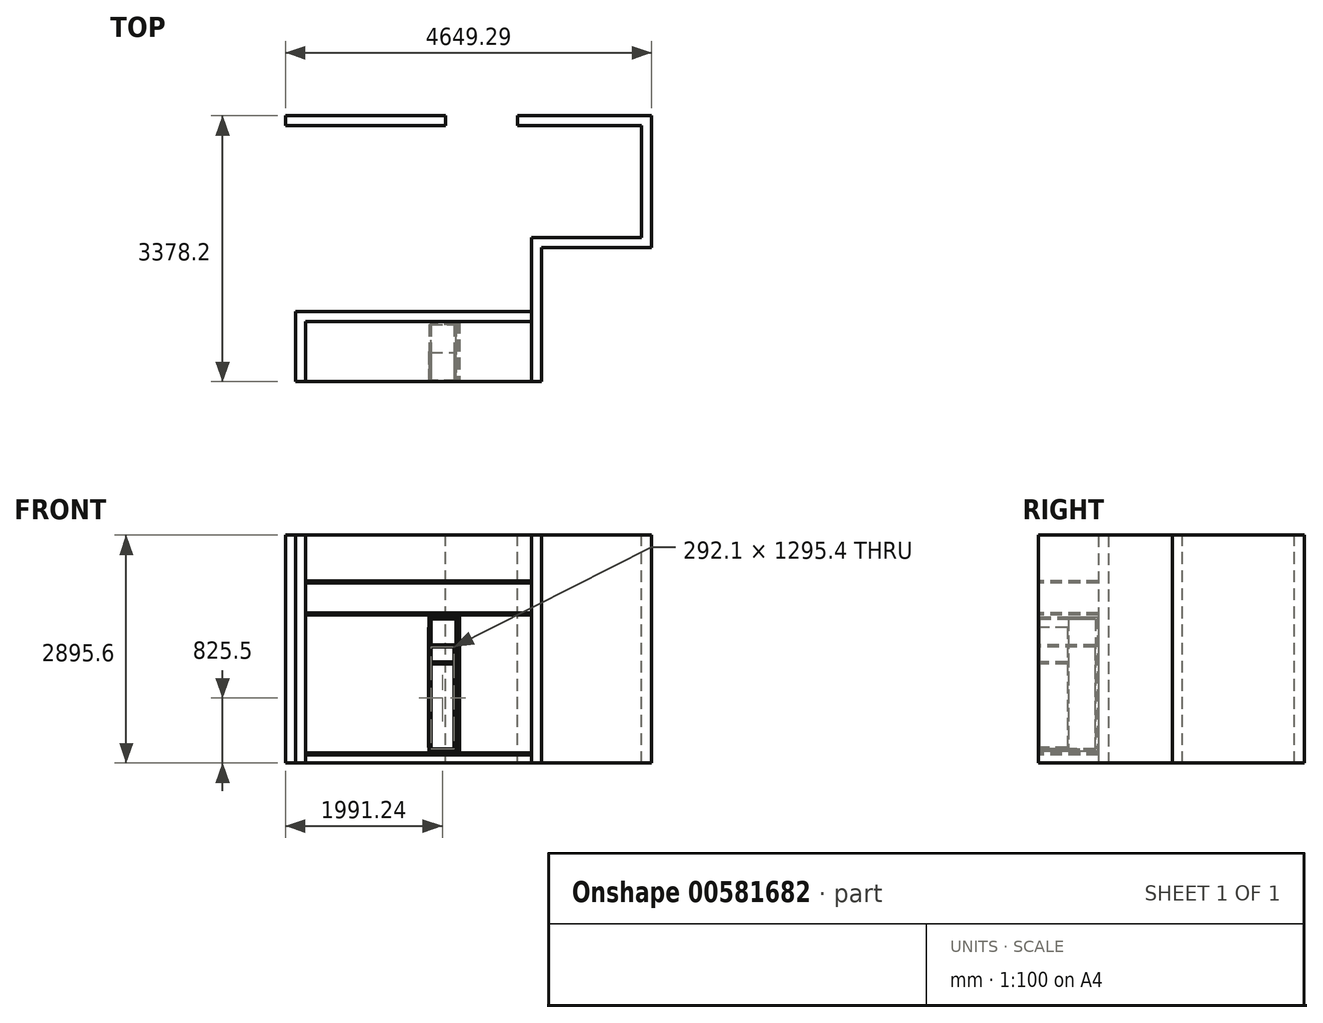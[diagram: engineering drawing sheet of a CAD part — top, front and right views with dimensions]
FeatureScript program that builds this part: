
annotation { "Feature Type Name" : "Feature", "Feature Type Description" : "" }
export const myFeature = defineFeature(function(context is Context, id is Id, definition is map)
    precondition{}
    {
        {
            var Q0;
            Q0=qCreatedBy(makeId("Top.planeOp"),FACE);
            var sketch = newSketch(context, id + "F0", { "sketchPlane" : qUnion([Q0])});
            skLineSegment(sketch, "E0.bottom", {"start": v(-1072.65, 1.26) * mm, "end": v(1797.55, 1.26) * mm});
            skLineSegment(sketch, "E0.top", {"start": v(-1072.65, -125.74) * mm, "end": v(1797.55, -125.74) * mm});
            skLineSegment(sketch, "E0.left", {"start": v(-1072.65, 1.26) * mm, "end": v(-1072.65, -125.74) * mm});
            skLineSegment(sketch, "E0.right", {"start": v(1797.55, 1.26) * mm, "end": v(1797.55, -125.74) * mm});
            skLineSegment(sketch, "E1.bottom", {"start": v(-1072.65, 1.26) * mm, "end": v(-1199.65, 1.26) * mm});
            skLineSegment(sketch, "E1.top", {"start": v(-1072.65, -887.74) * mm, "end": v(-1199.65, -887.74) * mm});
            skLineSegment(sketch, "E1.left", {"start": v(-1072.65, 1.26) * mm, "end": v(-1072.65, -887.74) * mm});
            skLineSegment(sketch, "E1.right", {"start": v(-1199.65, 1.26) * mm, "end": v(-1199.65, -887.74) * mm});
            skSolve(sketch);
        }
        {
            var Q0;
            {var subQ3=sQuery(id+"F0.wireOp",EDGE,"E1.bottom");Q0=makeQuery(id+"F0.imprint","IMPRINT",FACE,{"disambiguationData":[TD([[makeQuery(id+"F0.imprint","IMPRINT",EDGE,{"derivedFrom":subQ3}),1.0]])]});}
            var Q1;
            {var subQ0=sQuery(id+"F0.wireOp",EDGE,"E0.bottom");Q1=makeQuery(id+"F0.imprint","IMPRINT",FACE,{"disambiguationData":[TD([[makeQuery(id+"F0.imprint","IMPRINT",EDGE,{"derivedFrom":subQ0}),-1.0]])]});}
            extrude(context, id + "F1", {"entities" : qUnion([Q0, Q1]), "depth" : 2895.6 * mm, "offsetDistance" : 25.4 * mm});
        }
        {
            var Q0;
            Q0=makeQuery(id+"F1.opExtrude","CAP_FACE",FACE,{"disambiguationData":[OSD([sQuery(id+"F0.wireOp",EDGE,"E0.bottom"),sQuery(id+"F0.wireOp",EDGE,"E0.top"),sQuery(id+"F0.wireOp",EDGE,"E0.right"),sQuery(id+"F0.wireOp",EDGE,"E1.bottom"),sQuery(id+"F0.wireOp",EDGE,"E1.top"),sQuery(id+"F0.wireOp",EDGE,"E1.left"),sQuery(id+"F0.wireOp",EDGE,"E1.right")])],"isStart":false});
            var sketch = newSketch(context, id + "F2", { "sketchPlane" : qUnion([Q0])});
            skLineSegment(sketch, "E2.bottom", {"start": v(-1072.65, -125.74) * mm, "end": v(1797.55, -125.74) * mm});
            skLineSegment(sketch, "E2.top", {"start": v(-1072.65, -887.74) * mm, "end": v(1797.55, -887.74) * mm});
            skLineSegment(sketch, "E2.left", {"start": v(-1072.65, -125.74) * mm, "end": v(-1072.65, -887.74) * mm});
            skLineSegment(sketch, "E2.right", {"start": v(1797.55, -125.74) * mm, "end": v(1797.55, -887.74) * mm});
            skSolve(sketch);
        }
        {
            var Q0;
            Q0=makeQuery(id+"F2.imprint","IMPRINT",FACE,{"disambiguationData":[TD([[makeQuery(id+"F2.imprint","IMPRINT",EDGE,{"derivedFrom":sQuery(id+"F2.wireOp",EDGE,"E2.bottom")}),-1.0]])]});
            extrude(context, id + "F3", {"entities" : qUnion([Q0]), "operationType" : NewBodyOperationType.ADD, "depth" : 25.4 * mm, "offsetDistance" : 25.4 * mm});
        }
        {
            var Q0;
            Q0=makeQuery(id+"F3.opExtrude","SWEPT_BODY",BODY,{"disambiguationData":[OSD([sQuery(id+"F2.wireOp",EDGE,"E2.bottom"),sQuery(id+"F2.wireOp",EDGE,"E2.top"),sQuery(id+"F2.wireOp",EDGE,"E2.left"),sQuery(id+"F2.wireOp",EDGE,"E2.right")])]});
            transform(context, id + "F4", {"entities" : qUnion([Q0]), "transformType" : TransformType.TRANSLATION_3D, "dx" : 0 * mm, "dy" : 0 * mm, "dz" : -609.6 * mm, "makeCopy" : false});
        }
        {
            var Q0;
            Q0=makeQuery(id+"F3.opExtrude","SWEPT_BODY",BODY,{"disambiguationData":[OSD([sQuery(id+"F2.wireOp",EDGE,"E2.bottom"),sQuery(id+"F2.wireOp",EDGE,"E2.top"),sQuery(id+"F2.wireOp",EDGE,"E2.left"),sQuery(id+"F2.wireOp",EDGE,"E2.right")])]});
            transform(context, id + "F5", {"entities" : qUnion([Q0]), "transformType" : TransformType.TRANSLATION_3D, "dx" : 0 * mm, "dy" : 0 * mm, "dz" : -406.4 * mm, "makeCopy" : true});
        }
        {
            var Q0;
            Q0=makeQuery(id+"F5.opPattern","COPY",FACE,{"derivedFrom":makeQuery(id+"F3.opExtrude","SWEPT_FACE",FACE,{"disambiguationData":[OSD([sQuery(id+"F2.wireOp",EDGE,"E2.top")])]}),"instanceName":"1"});
            var sketch = newSketch(context, id + "F6", { "sketchPlane" : qUnion([Q0])});
            skLineSegment(sketch, "E3.bottom", {"start": v(793.61, 1879.6) * mm, "end": v(819.01, 1879.6) * mm});
            skLineSegment(sketch, "E3.top", {"start": v(793.61, 127) * mm, "end": v(819.01, 127) * mm});
            skLineSegment(sketch, "E3.left", {"start": v(793.61, 1879.6) * mm, "end": v(793.61, 127) * mm});
            skLineSegment(sketch, "E3.right", {"start": v(819.01, 1879.6) * mm, "end": v(819.01, 127) * mm});
            skSolve(sketch);
        }
        {
            var Q0;
            Q0=makeQuery(id+"F6.imprint","IMPRINT",FACE,{"disambiguationData":[TD([[makeQuery(id+"F6.imprint","IMPRINT",EDGE,{"derivedFrom":sQuery(id+"F6.wireOp",EDGE,"E3.bottom")}),-1.0]])]});
            extrude(context, id + "F7", {"entities" : qUnion([Q0]), "depth" : -762 * mm, "offsetDistance" : 25.4 * mm});
        }
        {
            var Q0;
            Q0=makeQuery(id+"F5.opPattern","COPY",BODY,{"derivedFrom":makeQuery(id+"F3.opExtrude","SWEPT_BODY",BODY,{"disambiguationData":[OSD([sQuery(id+"F2.wireOp",EDGE,"E2.bottom"),sQuery(id+"F2.wireOp",EDGE,"E2.top"),sQuery(id+"F2.wireOp",EDGE,"E2.left"),sQuery(id+"F2.wireOp",EDGE,"E2.right")])]}),"instanceName":"1"});
            transform(context, id + "F8", {"entities" : qUnion([Q0]), "transformType" : TransformType.TRANSLATION_3D, "dx" : 0 * mm, "dy" : 0 * mm, "dz" : -1778 * mm, "makeCopy" : true});
        }
        {
            var Q0;
            Q0=makeQuery(id+"F7.opExtrude","SWEPT_BODY",BODY,{"disambiguationData":[OSD([sQuery(id+"F6.wireOp",EDGE,"E3.bottom"),sQuery(id+"F6.wireOp",EDGE,"E3.top"),sQuery(id+"F6.wireOp",EDGE,"E3.left"),sQuery(id+"F6.wireOp",EDGE,"E3.right")])]});
            transform(context, id + "F9", {"entities" : qUnion([Q0]), "transformType" : TransformType.TRANSLATION_3D, "dx" : 64.13 * mm, "dy" : 0 * mm, "dz" : 0 * mm, "makeCopy" : false});
        }
        {
            var Q0;
            Q0=makeQuery(id+"F8.opPattern","COPY",FACE,{"derivedFrom":makeQuery(id+"F5.opPattern","COPY",FACE,{"derivedFrom":makeQuery(id+"F3.opExtrude","CAP_FACE",FACE,{"disambiguationData":[OSD([sQuery(id+"F2.wireOp",EDGE,"E2.bottom"),sQuery(id+"F2.wireOp",EDGE,"E2.top"),sQuery(id+"F2.wireOp",EDGE,"E2.left"),sQuery(id+"F2.wireOp",EDGE,"E2.right")])],"isStart":false}),"instanceName":"1"}),"instanceName":"1"});
            var sketch = newSketch(context, id + "F10", { "sketchPlane" : qUnion([Q0])});
            skLineSegment(sketch, "E4.bottom", {"start": v(831.7, -876.48) * mm, "end": v(488.8, -876.48) * mm});
            skLineSegment(sketch, "E4.top", {"start": v(831.7, -139.88) * mm, "end": v(488.8, -139.88) * mm});
            skLineSegment(sketch, "E4.left", {"start": v(831.7, -876.48) * mm, "end": v(831.7, -139.88) * mm});
            skLineSegment(sketch, "E4.right", {"start": v(488.8, -876.48) * mm, "end": v(488.8, -139.88) * mm});
            skSolve(sketch);
        }
        {
            var Q0;
            Q0=makeQuery(id+"F10.imprint","IMPRINT",FACE,{"disambiguationData":[TD([[makeQuery(id+"F10.imprint","IMPRINT",EDGE,{"derivedFrom":sQuery(id+"F10.wireOp",EDGE,"E4.bottom")}),-1.0]])]});
            extrude(context, id + "F11", {"entities" : qUnion([Q0]), "depth" : 1701.8 * mm, "offsetDistance" : 25.4 * mm});
        }
        {
            var Q0;
            Q0=makeQuery(id+"F11.opExtrude","SWEPT_BODY",BODY,{"disambiguationData":[OSD([sQuery(id+"F10.wireOp",EDGE,"E4.bottom"),sQuery(id+"F10.wireOp",EDGE,"E4.top"),sQuery(id+"F10.wireOp",EDGE,"E4.left"),sQuery(id+"F10.wireOp",EDGE,"E4.right")])]});
            transform(context, id + "F12", {"entities" : qUnion([Q0]), "transformType" : TransformType.TRANSLATION_3D, "dx" : 3.25 * mm, "dy" : 0 * mm, "dz" : 25.4 * mm, "makeCopy" : false});
        }
        {
            var Q0;
            Q0=makeQuery(id+"F11.opExtrude","SWEPT_FACE",FACE,{"disambiguationData":[OSD([sQuery(id+"F10.wireOp",EDGE,"E4.bottom")])]});
            shell(context, id + "F13", {"entities" : qUnion([Q0]), "thickness" : 25.4 * mm});
        }
        {
            var Q0;
            Q0=makeQuery(id+"F11.opExtrude","SWEPT_FACE",FACE,{"disambiguationData":[OSD([sQuery(id+"F10.wireOp",EDGE,"E4.right")])]});
            var sketch = newSketch(context, id + "F14", { "sketchPlane" : qUnion([Q0])});
            skLineSegment(sketch, "E5.bottom", {"start": v(139.88, 1854.2) * mm, "end": v(508.18, 1854.2) * mm});
            skLineSegment(sketch, "E5.top", {"start": v(139.88, 152.4) * mm, "end": v(508.18, 152.4) * mm});
            skLineSegment(sketch, "E5.left", {"start": v(139.88, 1854.2) * mm, "end": v(139.88, 152.4) * mm});
            skLineSegment(sketch, "E5.right", {"start": v(508.18, 1854.2) * mm, "end": v(508.18, 152.4) * mm});
            skSolve(sketch);
        }
        {
            var Q0;
            Q0=makeQuery(id+"F14.imprint","IMPRINT",FACE,{"disambiguationData":[TD([[makeQuery(id+"F14.imprint","IMPRINT",EDGE,{"derivedFrom":sQuery(id+"F14.wireOp",EDGE,"E5.bottom")}),1.0]])]});
            extrude(context, id + "F15", {"entities" : qUnion([Q0]), "operationType" : NewBodyOperationType.REMOVE, "oppositeDirection" : true, "depth" : 25.4 * mm, "offsetDistance" : 25.4 * mm});
        }
        {
            var Q0;
            Q0=makeQuery(id+"F13.opShell","OFFSET_FACE",FACE,{"disambiguationData":[OSD([sQuery(id+"F10.wireOp",EDGE,"E4.left")])]});
            extrude(context, id + "F16", {"entities" : qUnion([Q0]), "operationType" : NewBodyOperationType.REMOVE, "oppositeDirection" : true, "depth" : 25.4 * mm, "offsetDistance" : 25.4 * mm});
        }
        {
            var Q0;
            Q0=makeQuery(id+"F11.opExtrude","SWEPT_FACE",FACE,{"disambiguationData":[OSD([sQuery(id+"F10.wireOp",EDGE,"E4.right")])]});
            var sketch = newSketch(context, id + "F17", { "sketchPlane" : qUnion([Q0])});
            skLineSegment(sketch, "E6.bottom", {"start": v(1637.69, 1724.74) * mm, "end": v(1993.29, 1724.74) * mm});
            skLineSegment(sketch, "E6.top", {"start": v(1637.69, 200.74) * mm, "end": v(1993.29, 200.74) * mm});
            skLineSegment(sketch, "E6.left", {"start": v(1637.69, 1724.74) * mm, "end": v(1637.69, 200.74) * mm});
            skLineSegment(sketch, "E6.right", {"start": v(1993.29, 1724.74) * mm, "end": v(1993.29, 200.74) * mm});
            skSolve(sketch);
        }
        {
            var Q0;
            Q0=makeQuery(id+"F17.imprint","IMPRINT",FACE,{"disambiguationData":[TD([[makeQuery(id+"F17.imprint","IMPRINT",EDGE,{"derivedFrom":sQuery(id+"F17.wireOp",EDGE,"E6.bottom")}),-1.0]])]});
            extrude(context, id + "F18", {"entities" : qUnion([Q0]), "depth" : 6.35 * mm, "offsetDistance" : 25.4 * mm});
        }
        {
            var Q0;
            Q0=makeQuery(id+"F18.opExtrude","SWEPT_BODY",BODY,{"disambiguationData":[OSD([sQuery(id+"F17.wireOp",EDGE,"E6.bottom"),sQuery(id+"F17.wireOp",EDGE,"E6.top"),sQuery(id+"F17.wireOp",EDGE,"E6.left"),sQuery(id+"F17.wireOp",EDGE,"E6.right")])]});
            transform(context, id + "F19", {"entities" : qUnion([Q0]), "transformType" : TransformType.TRANSLATION_3D, "dx" : 0 * mm, "dy" : 1117.6 * mm, "dz" : 0 * mm, "makeCopy" : false});
        }
        {
            var Q0;
            Q0=makeQuery(id+"F11.opExtrude","SWEPT_FACE",FACE,{"disambiguationData":[OSD([sQuery(id+"F10.wireOp",EDGE,"E4.bottom")])]});
            var sketch = newSketch(context, id + "F20", { "sketchPlane" : qUnion([Q0])});
            skLineSegment(sketch, "E7.bottom", {"start": v(1040.15, 152.4) * mm, "end": v(1383.05, 152.4) * mm});
            skLineSegment(sketch, "E7.top", {"start": v(1040.15, 1498.6) * mm, "end": v(1383.05, 1498.6) * mm});
            skLineSegment(sketch, "E7.left", {"start": v(1040.15, 152.4) * mm, "end": v(1040.15, 1498.6) * mm});
            skLineSegment(sketch, "E7.right", {"start": v(1383.05, 152.4) * mm, "end": v(1383.05, 1498.6) * mm});
            skSolve(sketch);
        }
        {
            var Q0;
            Q0 = qSketchRegion(id + "F20", true);
            extrude(context, id + "F21", {"entities" : qUnion([Q0]), "operationType" : NewBodyOperationType.ADD, "depth" : -711.2 * mm, "offsetDistance" : 25.4 * mm});
        }
        {
            var Q0;
            Q0=makeQuery(id+"F21.opExtrude","CAP_FACE",FACE,{"disambiguationData":[OSD([sQuery(id+"F20.wireOp",EDGE,"E7.bottom"),sQuery(id+"F20.wireOp",EDGE,"E7.top"),sQuery(id+"F20.wireOp",EDGE,"E7.left"),sQuery(id+"F20.wireOp",EDGE,"E7.right")])],"isStart":true});
            shell(context, id + "F22", {"entities" : qUnion([Q0]), "thickness" : 25.4 * mm});
        }
        {
            var Q0;
            Q0=makeQuery(id+"F22.opShell","OFFSET_FACE",FACE,{"disambiguationData":[OSD([sQuery(id+"F20.wireOp",EDGE,"E7.bottom"),sQuery(id+"F20.wireOp",EDGE,"E7.top"),sQuery(id+"F20.wireOp",EDGE,"E7.left"),sQuery(id+"F20.wireOp",EDGE,"E7.right")])]});
            extrude(context, id + "F23", {"entities" : qUnion([Q0]), "operationType" : NewBodyOperationType.REMOVE, "oppositeDirection" : true, "depth" : 25.4 * mm, "offsetDistance" : 25.4 * mm});
        }
        {
            var Q0;
            Q0=makeQuery(id+"F21.opExtrude","SWEPT_BODY",BODY,{"disambiguationData":[OSD([sQuery(id+"F20.wireOp",EDGE,"E7.bottom"),sQuery(id+"F20.wireOp",EDGE,"E7.top"),sQuery(id+"F20.wireOp",EDGE,"E7.left"),sQuery(id+"F20.wireOp",EDGE,"E7.right")])]});
            transform(context, id + "F24", {"entities" : qUnion([Q0]), "transformType" : TransformType.TRANSLATION_3D, "dx" : -548.1 * mm, "dy" : 0 * mm, "dz" : 0 * mm, "makeCopy" : false});
        }
        {
            var Q0;
            Q0=makeQuery(id+"F11.opExtrude","SWEPT_FACE",FACE,{"disambiguationData":[OSD([sQuery(id+"F10.wireOp",EDGE,"E4.bottom")])]});
            var sketch = newSketch(context, id + "F25", { "sketchPlane" : qUnion([Q0])});
            skLineSegment(sketch, "E8.bottom", {"start": v(517.46, 1284.7) * mm, "end": v(809.56, 1284.7) * mm});
            skLineSegment(sketch, "E8.top", {"start": v(517.46, 1259.3) * mm, "end": v(809.56, 1259.3) * mm});
            skLineSegment(sketch, "E8.left", {"start": v(517.46, 1284.7) * mm, "end": v(517.46, 1259.3) * mm});
            skLineSegment(sketch, "E8.right", {"start": v(809.56, 1284.7) * mm, "end": v(809.56, 1259.3) * mm});
            skSolve(sketch);
        }
        {
            var Q0;
            Q0 = qSketchRegion(id + "F25", true);
            extrude(context, id + "F26", {"entities" : qUnion([Q0]), "depth" : -355.6 * mm, "offsetDistance" : 25.4 * mm});
        }
        {
            var Q0;
            Q0=makeQuery(id+"F1.opExtrude","CAP_FACE",FACE,{"disambiguationData":[OSD([sQuery(id+"F0.wireOp",EDGE,"E0.bottom"),sQuery(id+"F0.wireOp",EDGE,"E0.top"),sQuery(id+"F0.wireOp",EDGE,"E0.right"),sQuery(id+"F0.wireOp",EDGE,"E1.bottom"),sQuery(id+"F0.wireOp",EDGE,"E1.top"),sQuery(id+"F0.wireOp",EDGE,"E1.left"),sQuery(id+"F0.wireOp",EDGE,"E1.right")])],"isStart":false});
            var sketch = newSketch(context, id + "F27", { "sketchPlane" : qUnion([Q0])});
            skLineSegment(sketch, "E9.bottom", {"start": v(1797.55, -890.16) * mm, "end": v(1924.55, -890.16) * mm});
            skLineSegment(sketch, "E9.top", {"start": v(1797.55, 938.64) * mm, "end": v(1924.55, 938.64) * mm});
            skLineSegment(sketch, "E9.left", {"start": v(1797.55, -890.16) * mm, "end": v(1797.55, 938.64) * mm});
            skLineSegment(sketch, "E9.right", {"start": v(1924.55, -890.16) * mm, "end": v(1924.55, 938.64) * mm});
            skSolve(sketch);
        }
        {
            var Q0;
            {var subQ4=sQuery(id+"F27.wireOp",EDGE,"E9.bottom");Q0=makeQuery(id+"F27.imprint","IMPRINT",FACE,{"disambiguationData":[TD([[makeQuery(id+"F27.imprint","IMPRINT",EDGE,{"derivedFrom":subQ4}),1.0]])]});}
            extrude(context, id + "F28", {"entities" : qUnion([Q0]), "depth" : -2895.6 * mm, "offsetDistance" : 25.4 * mm});
        }
        {
            var Q0;
            Q0=makeQuery(id+"F28.opExtrude","CAP_FACE",FACE,{"disambiguationData":[OSD([sQuery(id+"F27.wireOp",EDGE,"E9.bottom"),sQuery(id+"F27.wireOp",EDGE,"E9.top"),sQuery(id+"F27.wireOp",EDGE,"E9.left"),sQuery(id+"F27.wireOp",EDGE,"E9.right")])],"isStart":true});
            var sketch = newSketch(context, id + "F29", { "sketchPlane" : qUnion([Q0])});
            skLineSegment(sketch, "E10.bottom", {"start": v(1924.55, 938.64) * mm, "end": v(3321.55, 938.64) * mm});
            skLineSegment(sketch, "E10.top", {"start": v(1924.55, 811.64) * mm, "end": v(3321.55, 811.64) * mm});
            skLineSegment(sketch, "E10.left", {"start": v(1924.55, 938.64) * mm, "end": v(1924.55, 811.64) * mm});
            skLineSegment(sketch, "E10.right", {"start": v(3321.55, 938.64) * mm, "end": v(3321.55, 811.64) * mm});
            skSolve(sketch);
        }
        {
            var Q0;
            Q0=makeQuery(id+"F29.imprint","IMPRINT",FACE,{"disambiguationData":[TD([[makeQuery(id+"F29.imprint","IMPRINT",EDGE,{"derivedFrom":sQuery(id+"F29.wireOp",EDGE,"E10.bottom")}),-1.0]])]});
            extrude(context, id + "F30", {"entities" : qUnion([Q0]), "operationType" : NewBodyOperationType.ADD, "depth" : -2895.6 * mm, "offsetDistance" : 25.4 * mm});
        }
        {
            var Q0;
            Q0=makeQuery(id+"F30.boolean.opBoolean","MERGE",FACE,{"derivedFrom":[makeQuery(id+"F28.opExtrude","CAP_FACE",FACE,{"disambiguationData":[OSD([sQuery(id+"F27.wireOp",EDGE,"E9.bottom"),sQuery(id+"F27.wireOp",EDGE,"E9.top"),sQuery(id+"F27.wireOp",EDGE,"E9.left"),sQuery(id+"F27.wireOp",EDGE,"E9.right")])],"isStart":true}),makeQuery(id+"F30.opExtrude","CAP_FACE",FACE,{"disambiguationData":[OSD([sQuery(id+"F29.wireOp",EDGE,"E10.bottom"),sQuery(id+"F29.wireOp",EDGE,"E10.top"),sQuery(id+"F29.wireOp",EDGE,"E10.left"),sQuery(id+"F29.wireOp",EDGE,"E10.right")])],"isStart":true})]});
            var sketch = newSketch(context, id + "F31", { "sketchPlane" : qUnion([Q0])});
            skLineSegment(sketch, "E11.bottom", {"start": v(3321.55, 938.64) * mm, "end": v(3194.55, 938.64) * mm});
            skLineSegment(sketch, "E11.top", {"start": v(3321.55, 2488.04) * mm, "end": v(3194.55, 2488.04) * mm});
            skLineSegment(sketch, "E11.left", {"start": v(3321.55, 938.64) * mm, "end": v(3321.55, 2488.04) * mm});
            skLineSegment(sketch, "E11.right", {"start": v(3194.55, 938.64) * mm, "end": v(3194.55, 2488.04) * mm});
            skSolve(sketch);
        }
        {
            var Q0;
            Q0=makeQuery(id+"F31.imprint","IMPRINT",FACE,{"disambiguationData":[TD([[makeQuery(id+"F31.imprint","IMPRINT",EDGE,{"derivedFrom":sQuery(id+"F31.wireOp",EDGE,"E11.bottom")}),1.0]])]});
            extrude(context, id + "F32", {"entities" : qUnion([Q0]), "operationType" : NewBodyOperationType.ADD, "depth" : -2895.6 * mm, "offsetDistance" : 25.4 * mm});
        }
        {
            var Q0;
            Q0=makeQuery(id+"F32.boolean.opBoolean","MERGE",FACE,{"derivedFrom":[makeQuery(id+"F30.boolean.opBoolean","MERGE",FACE,{"derivedFrom":[makeQuery(id+"F28.opExtrude","CAP_FACE",FACE,{"disambiguationData":[OSD([sQuery(id+"F27.wireOp",EDGE,"E9.bottom"),sQuery(id+"F27.wireOp",EDGE,"E9.top"),sQuery(id+"F27.wireOp",EDGE,"E9.left"),sQuery(id+"F27.wireOp",EDGE,"E9.right")])],"isStart":true}),makeQuery(id+"F30.opExtrude","CAP_FACE",FACE,{"disambiguationData":[OSD([sQuery(id+"F29.wireOp",EDGE,"E10.bottom"),sQuery(id+"F29.wireOp",EDGE,"E10.top"),sQuery(id+"F29.wireOp",EDGE,"E10.left"),sQuery(id+"F29.wireOp",EDGE,"E10.right")])],"isStart":true})]}),makeQuery(id+"F32.opExtrude","CAP_FACE",FACE,{"disambiguationData":[OSD([sQuery(id+"F31.wireOp",EDGE,"E11.bottom"),sQuery(id+"F31.wireOp",EDGE,"E11.top"),sQuery(id+"F31.wireOp",EDGE,"E11.left"),sQuery(id+"F31.wireOp",EDGE,"E11.right")])],"isStart":true})]});
            var sketch = newSketch(context, id + "F33", { "sketchPlane" : qUnion([Q0])});
            skLineSegment(sketch, "E12.bottom", {"start": v(3194.55, 2488.04) * mm, "end": v(1619.75, 2488.04) * mm});
            skLineSegment(sketch, "E12.top", {"start": v(3194.55, 2361.04) * mm, "end": v(1619.75, 2361.04) * mm});
            skLineSegment(sketch, "E12.left", {"start": v(3194.55, 2488.04) * mm, "end": v(3194.55, 2361.04) * mm});
            skLineSegment(sketch, "E12.right", {"start": v(1619.75, 2488.04) * mm, "end": v(1619.75, 2361.04) * mm});
            skSolve(sketch);
        }
        {
            var Q0;
            Q0=makeQuery(id+"F33.imprint","IMPRINT",FACE,{"disambiguationData":[TD([[makeQuery(id+"F33.imprint","IMPRINT",EDGE,{"derivedFrom":sQuery(id+"F33.wireOp",EDGE,"E12.bottom")}),1.0]])]});
            extrude(context, id + "F34", {"entities" : qUnion([Q0]), "operationType" : NewBodyOperationType.ADD, "depth" : -2895.6 * mm, "offsetDistance" : 25.4 * mm});
        }
        {
            var Q0;
            Q0=makeQuery(id+"F34.boolean.opBoolean","MERGE",FACE,{"derivedFrom":[makeQuery(id+"F32.boolean.opBoolean","MERGE",FACE,{"derivedFrom":[makeQuery(id+"F30.boolean.opBoolean","MERGE",FACE,{"derivedFrom":[makeQuery(id+"F28.opExtrude","CAP_FACE",FACE,{"disambiguationData":[OSD([sQuery(id+"F27.wireOp",EDGE,"E9.bottom"),sQuery(id+"F27.wireOp",EDGE,"E9.top"),sQuery(id+"F27.wireOp",EDGE,"E9.left"),sQuery(id+"F27.wireOp",EDGE,"E9.right")])],"isStart":true}),makeQuery(id+"F30.opExtrude","CAP_FACE",FACE,{"disambiguationData":[OSD([sQuery(id+"F29.wireOp",EDGE,"E10.bottom"),sQuery(id+"F29.wireOp",EDGE,"E10.top"),sQuery(id+"F29.wireOp",EDGE,"E10.left"),sQuery(id+"F29.wireOp",EDGE,"E10.right")])],"isStart":true})]}),makeQuery(id+"F32.opExtrude","CAP_FACE",FACE,{"disambiguationData":[OSD([sQuery(id+"F31.wireOp",EDGE,"E11.bottom"),sQuery(id+"F31.wireOp",EDGE,"E11.top"),sQuery(id+"F31.wireOp",EDGE,"E11.left"),sQuery(id+"F31.wireOp",EDGE,"E11.right")])],"isStart":true})]}),makeQuery(id+"F34.opExtrude","CAP_FACE",FACE,{"disambiguationData":[OSD([sQuery(id+"F33.wireOp",EDGE,"E12.bottom"),sQuery(id+"F33.wireOp",EDGE,"E12.top"),sQuery(id+"F33.wireOp",EDGE,"E12.left"),sQuery(id+"F33.wireOp",EDGE,"E12.right")])],"isStart":true})]});
            var sketch = newSketch(context, id + "F35", { "sketchPlane" : qUnion([Q0])});
            skLineSegment(sketch, "E13.bottom", {"start": v(838.88, 2361.04) * mm, "end": v(-1193.12, 2361.04) * mm});
            skLineSegment(sketch, "E13.top", {"start": v(838.88, 2488.04) * mm, "end": v(-1193.12, 2488.04) * mm});
            skLineSegment(sketch, "E13.left", {"start": v(838.88, 2361.04) * mm, "end": v(838.88, 2488.04) * mm});
            skLineSegment(sketch, "E13.right", {"start": v(-1193.12, 2361.04) * mm, "end": v(-1193.12, 2488.04) * mm});
            skSolve(sketch);
        }
        {
            var Q0;
            Q0=makeQuery(id+"F35.imprint","IMPRINT",FACE,{"disambiguationData":[TD([[makeQuery(id+"F35.imprint","IMPRINT",EDGE,{"derivedFrom":sQuery(id+"F35.wireOp",EDGE,"E13.bottom")}),-1.0]])]});
            extrude(context, id + "F36", {"entities" : qUnion([Q0]), "depth" : -2895.6 * mm, "offsetDistance" : 25.4 * mm});
        }
        {
            var Q0;
            Q0=makeQuery(id+"F36.opExtrude","SWEPT_BODY",BODY,{"disambiguationData":[OSD([sQuery(id+"F35.wireOp",EDGE,"E13.bottom"),sQuery(id+"F35.wireOp",EDGE,"E13.top"),sQuery(id+"F35.wireOp",EDGE,"E13.left"),sQuery(id+"F35.wireOp",EDGE,"E13.right")])]});
            transform(context, id + "F37", {"entities" : qUnion([Q0]), "transformType" : TransformType.TRANSLATION_3D, "dx" : -134.62 * mm, "dy" : 0 * mm, "dz" : 0 * mm, "makeCopy" : false});
        }
    });
